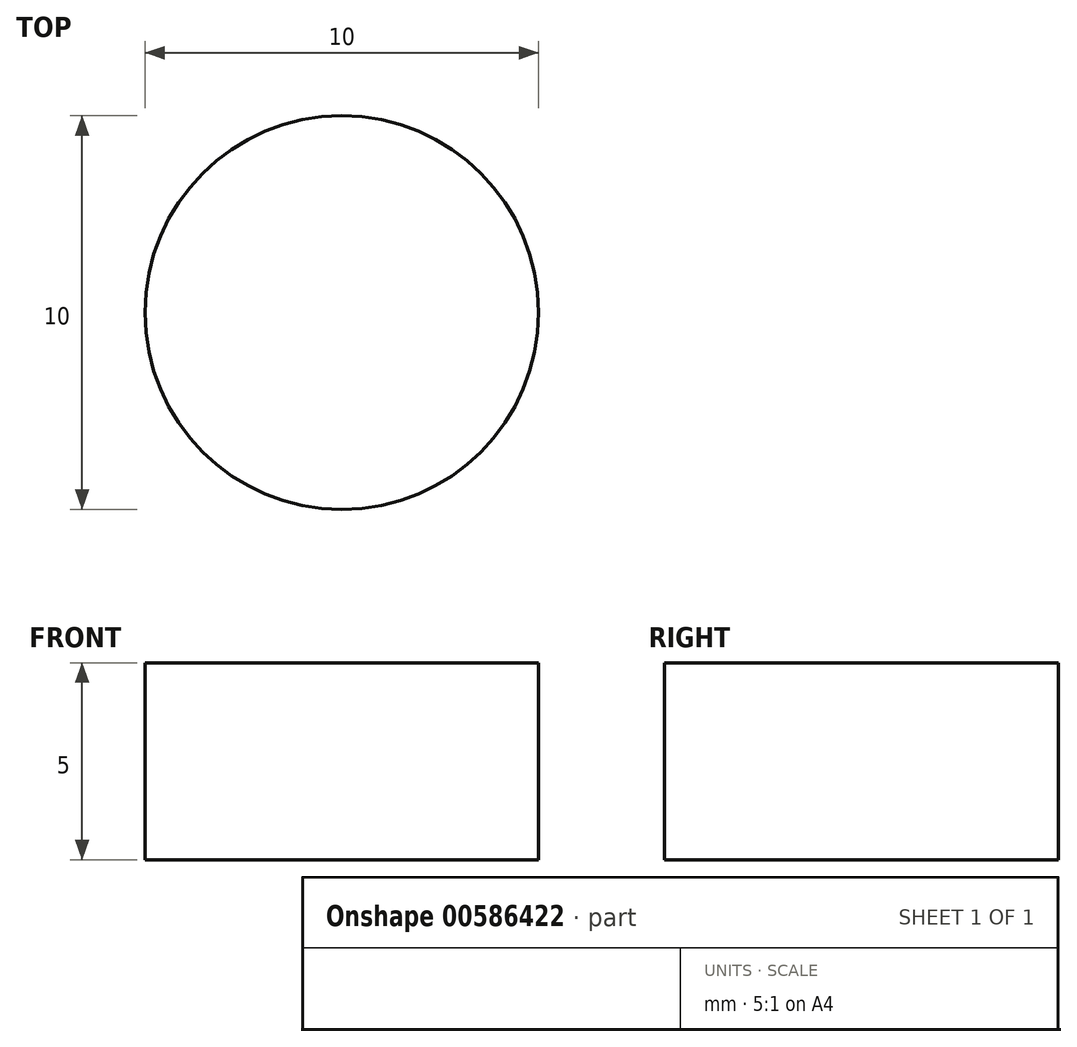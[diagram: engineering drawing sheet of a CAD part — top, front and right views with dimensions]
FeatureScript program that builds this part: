
annotation { "Feature Type Name" : "Feature", "Feature Type Description" : "" }
export const myFeature = defineFeature(function(context is Context, id is Id, definition is map)
    precondition{}
    {
        {
            var Q0;
            Q0=qCreatedBy(makeId("Top.planeOp"),FACE);
            var sketch = newSketch(context, id + "F0", { "sketchPlane" : qUnion([Q0])});
            skCircle(sketch, "E0", {"center": v(0, 0) * mm, "radius": 5 * mm});
            skSolve(sketch);
        }
        {
            var Q0;
            Q0=qSketchRegion(id+"F0",true);
            extrude(context, id + "F1", {"entities" : qUnion([Q0]), "depth" : 5 * mm, "offsetDistance" : 25 * mm});
        }
    });
